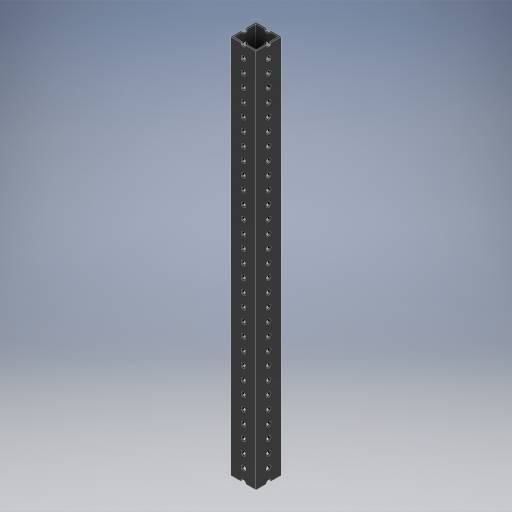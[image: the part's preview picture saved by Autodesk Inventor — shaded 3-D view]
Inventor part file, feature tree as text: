
AUTODESK INVENTOR PART (.ipt)
format: ipt  version: 2024.2 (Build 282272000, 272)  size: 508,928 bytes
history: native  units: in
note: dims shown in document units (in); Inventor stores cm internally (conversion verified against a paired STEP export)
features: projected_geometry x8, other x4, extrude x1, sketch x1
ambient origin geometry x8: Origin, YZ Plane, XZ Plane, XY Plane, X Axis, Y Axis, Z Axis, Center Point
bodies: Body1 (feature_tree)
feature tree (14):
  other  "2024-210-003-Front-Angle"
  other  "2024-210-000-Fixed-Shootaur.ipt"
  extrude  "Extrusion1"  Depth=0.3937in TaperAngle=0.0deg
  other  "2024-210-003-Front-Angle::2024-210-000-Fixed-Shootaur.ipt"
  other  "TaggingFeature1"
  sketch  "Sketch1"  dims[d0=0.3937in d1=0.5in d2=0.0in]
  projected_geometry  "Projected Loop1"
  projected_geometry  "Projected Loop2"
  projected_geometry  "Projected Loop3"
  projected_geometry  "Projected Loop4"
  projected_geometry  "Projected Loop5"
  projected_geometry  "Projected Loop6"
  projected_geometry  "Projected Loop7"
  projected_geometry  "Projected Loop8"
